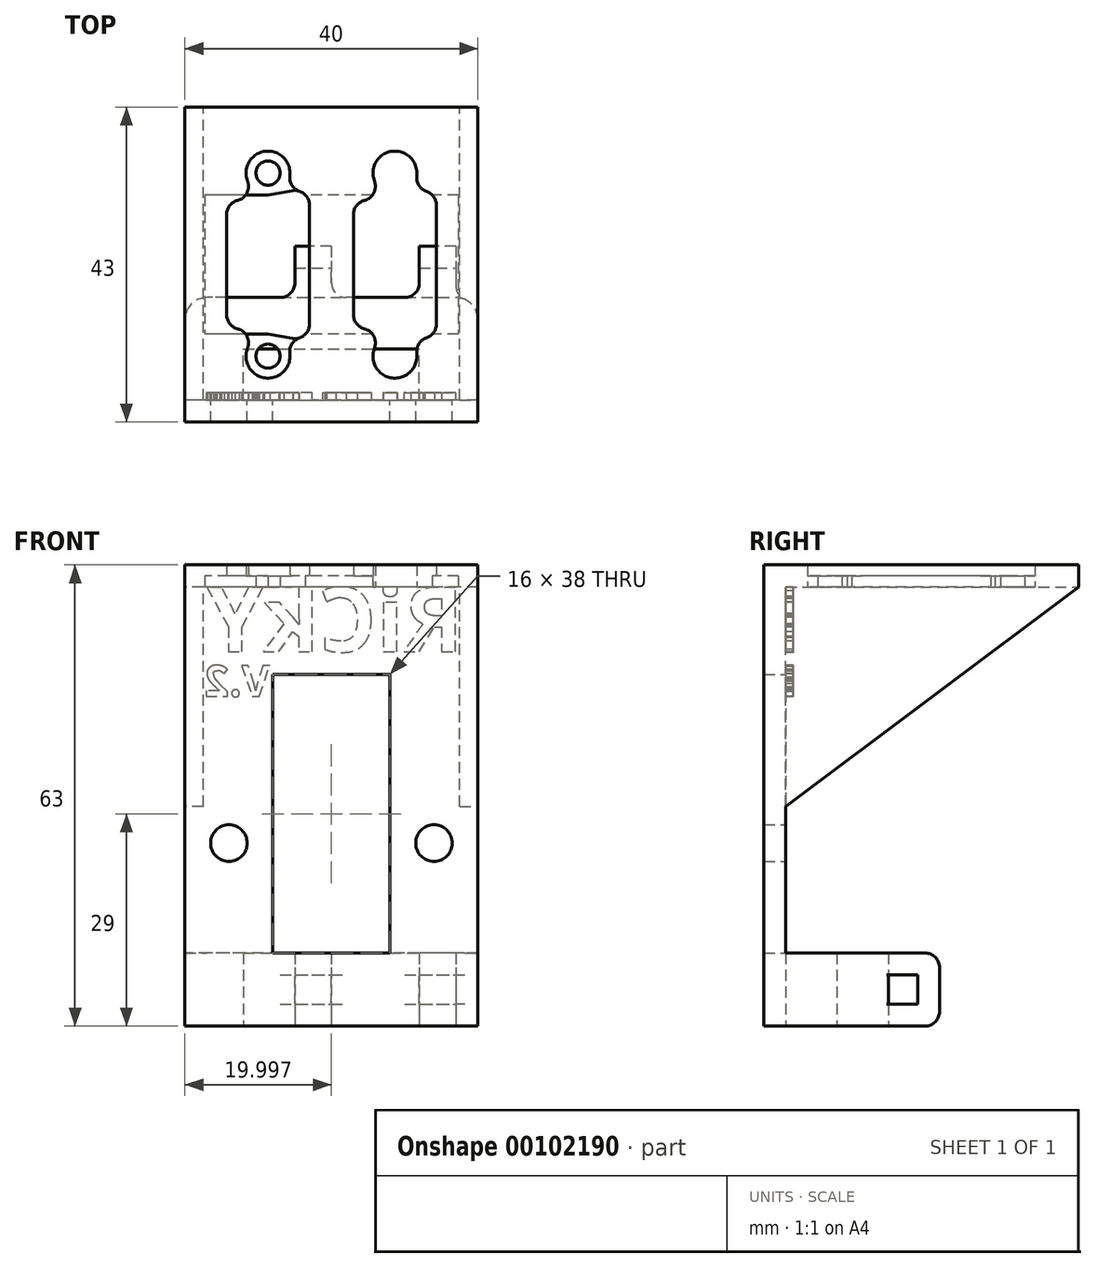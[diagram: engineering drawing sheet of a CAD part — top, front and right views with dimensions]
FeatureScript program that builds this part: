
annotation { "Feature Type Name" : "Feature", "Feature Type Description" : "" }
export const myFeature = defineFeature(function(context is Context, id is Id, definition is map)
    precondition{}
    {
        {
            var Q0;
            Q0=qCreatedBy(makeId("Top.planeOp"),FACE);
            var sketch = newSketch(context, id + "F0", { "sketchPlane" : qUnion([Q0])});
            skLineSegment(sketch, "E0", {"start": v(-4.26, 15.16) * mm, "end": v(16.74, 15.16) * mm});
            skLineSegment(sketch, "E1", {"start": v(-2.26, 3.83) * mm, "end": v(14.74, 3.83) * mm});
            skLineSegment(sketch, "E2", {"start": v(14.74, 3.83) * mm, "end": v(16.74, 15.16) * mm});
            skLineSegment(sketch, "E3", {"start": v(-2.26, 3.83) * mm, "end": v(-4.26, 15.16) * mm});
            skPoint(sketch, "E4", {"position": v(-3.26, 9.5) * mm});
            skPoint(sketch, "E5", {"position": v(15.74, 9.5) * mm});
            skPoint(sketch, "E6", {"position": v(-6.26, 9.5) * mm});
            skPoint(sketch, "E7", {"position": v(18.74, 9.5) * mm});
            skCircle(sketch, "E8", {"center": v(-6.26, 9.5) * mm, "radius": 3 * mm});
            skCircle(sketch, "E9", {"center": v(18.74, 9.5) * mm, "radius": 3 * mm});
            skLineSegment(sketch, "E10", {"start": v(-4.26, 32.48) * mm, "end": v(16.74, 32.48) * mm});
            skLineSegment(sketch, "E11", {"start": v(-2.26, 21.16) * mm, "end": v(14.74, 21.16) * mm});
            skLineSegment(sketch, "E12", {"start": v(14.74, 21.16) * mm, "end": v(16.74, 32.48) * mm});
            skLineSegment(sketch, "E13", {"start": v(-2.26, 21.16) * mm, "end": v(-4.26, 32.48) * mm});
            skPoint(sketch, "E14", {"position": v(-3.26, 26.82) * mm});
            skPoint(sketch, "E15", {"position": v(15.74, 26.82) * mm});
            skPoint(sketch, "E16", {"position": v(-6.26, 26.82) * mm});
            skPoint(sketch, "E17", {"position": v(18.74, 26.82) * mm});
            skCircle(sketch, "E18", {"center": v(-6.26, 26.82) * mm, "radius": 3 * mm});
            skCircle(sketch, "E19", {"center": v(18.74, 26.82) * mm, "radius": 3 * mm});
            skLineSegment(sketch, "E20.bottom", {"start": v(27.74, 38.16) * mm, "end": v(-15.26, 38.16) * mm});
            skLineSegment(sketch, "E20.top", {"start": v(27.74, -1.84) * mm, "end": v(-15.26, -1.84) * mm});
            skLineSegment(sketch, "E20.left", {"start": v(27.74, 38.16) * mm, "end": v(27.74, -1.84) * mm});
            skLineSegment(sketch, "E20.right", {"start": v(-15.26, 38.16) * mm, "end": v(-15.26, -1.84) * mm});
            skLineSegment(sketch, "E21", {"start": v(-6.26, 12.5) * mm, "end": v(-3.8, 12.5) * mm});
            skLineSegment(sketch, "E22", {"start": v(-6.26, 6.5) * mm, "end": v(-2.73, 6.5) * mm});
            skLineSegment(sketch, "E23", {"start": v(18.74, 12.5) * mm, "end": v(16.27, 12.5) * mm});
            skLineSegment(sketch, "E24", {"start": v(18.74, 6.5) * mm, "end": v(15.2, 6.5) * mm});
            skLineSegment(sketch, "E25", {"start": v(18.74, 29.82) * mm, "end": v(16.27, 29.82) * mm});
            skLineSegment(sketch, "E26", {"start": v(18.74, 23.82) * mm, "end": v(15.2, 23.82) * mm});
            skLineSegment(sketch, "E27", {"start": v(-6.26, 29.82) * mm, "end": v(-3.8, 29.82) * mm});
            skLineSegment(sketch, "E28", {"start": v(-6.26, 23.82) * mm, "end": v(-2.73, 23.82) * mm});
            skSolve(sketch);
        }
        {
            var Q0;
            Q0=makeQuery(id+"F0.imprint","IMPRINT",FACE,{"disambiguationData":[TD([[makeQuery(id+"F0.imprint","IMPRINT",EDGE,{"derivedFrom":sQuery(id+"F0.wireOp",EDGE,"E0")}),1.0]])]});
            var Q1;
            {var subQ0=sQuery(id+"F0.wireOp",EDGE,"E26");Q1=makeQuery(id+"F0.imprint","IMPRINT",FACE,{"disambiguationData":[TD([[makeQuery(id+"F0.imprint","IMPRINT",EDGE,{"derivedFrom":subQ0}),-1.0]])]});}
            var Q2;
            {var subQ0=sQuery(id+"F0.wireOp",EDGE,"E25");Q2=makeQuery(id+"F0.imprint","IMPRINT",FACE,{"disambiguationData":[TD([[makeQuery(id+"F0.imprint","IMPRINT",EDGE,{"derivedFrom":subQ0}),1.0]])]});}
            var Q3;
            {var subQ0=sQuery(id+"F0.wireOp",EDGE,"E24");Q3=makeQuery(id+"F0.imprint","IMPRINT",FACE,{"disambiguationData":[TD([[makeQuery(id+"F0.imprint","IMPRINT",EDGE,{"derivedFrom":subQ0}),-1.0]])]});}
            var Q4;
            {var subQ0=sQuery(id+"F0.wireOp",EDGE,"E23");Q4=makeQuery(id+"F0.imprint","IMPRINT",FACE,{"disambiguationData":[TD([[makeQuery(id+"F0.imprint","IMPRINT",EDGE,{"derivedFrom":subQ0}),1.0]])]});}
            var Q5;
            {var subQ0=sQuery(id+"F0.wireOp",EDGE,"E28");Q5=makeQuery(id+"F0.imprint","IMPRINT",FACE,{"disambiguationData":[TD([[makeQuery(id+"F0.imprint","IMPRINT",EDGE,{"derivedFrom":subQ0}),1.0]])]});}
            var Q6;
            {var subQ0=sQuery(id+"F0.wireOp",EDGE,"E27");Q6=makeQuery(id+"F0.imprint","IMPRINT",FACE,{"disambiguationData":[TD([[makeQuery(id+"F0.imprint","IMPRINT",EDGE,{"derivedFrom":subQ0}),-1.0]])]});}
            var Q7;
            {var subQ0=sQuery(id+"F0.wireOp",EDGE,"E22");Q7=makeQuery(id+"F0.imprint","IMPRINT",FACE,{"disambiguationData":[TD([[makeQuery(id+"F0.imprint","IMPRINT",EDGE,{"derivedFrom":subQ0}),1.0]])]});}
            var Q8;
            {var subQ0=sQuery(id+"F0.wireOp",EDGE,"E21");Q8=makeQuery(id+"F0.imprint","IMPRINT",FACE,{"disambiguationData":[TD([[makeQuery(id+"F0.imprint","IMPRINT",EDGE,{"derivedFrom":subQ0}),-1.0]])]});}
            extrude(context, id + "F1", {"entities" : qUnion([Q0, Q1, Q2, Q3, Q4, Q5, Q6, Q7, Q8]), "depth" : 3 * mm});
        }
        {
            var Q0;
            Q0=makeQuery(id+"F1.opExtrude","SWEPT_EDGE",EDGE,{"disambiguationData":[OSD([sQuery(id+"F0.wireOp",EDGE,"E0"),sQuery(id+"F0.wireOp",EDGE,"E3")])]});
            var Q1;
            Q1=makeQuery(id+"F1.opExtrude","SWEPT_EDGE",EDGE,{"disambiguationData":[OSD([sQuery(id+"F0.wireOp",EDGE,"E1"),sQuery(id+"F0.wireOp",EDGE,"E2")])]});
            var Q2;
            Q2=makeQuery(id+"F1.opExtrude","SWEPT_EDGE",EDGE,{"disambiguationData":[OSD([sQuery(id+"F0.wireOp",EDGE,"E0"),sQuery(id+"F0.wireOp",EDGE,"E2")])]});
            var Q3;
            Q3=makeQuery(id+"F1.opExtrude","SWEPT_EDGE",EDGE,{"disambiguationData":[OSD([sQuery(id+"F0.wireOp",EDGE,"E1"),sQuery(id+"F0.wireOp",EDGE,"E3")])]});
            var Q4;
            Q4=makeQuery(id+"F1.opExtrude","SWEPT_EDGE",EDGE,{"disambiguationData":[OSD([sQuery(id+"F0.wireOp",EDGE,"E10"),sQuery(id+"F0.wireOp",EDGE,"E13")])]});
            var Q5;
            Q5=makeQuery(id+"F1.opExtrude","SWEPT_EDGE",EDGE,{"disambiguationData":[OSD([sQuery(id+"F0.wireOp",EDGE,"E10"),sQuery(id+"F0.wireOp",EDGE,"E12")])]});
            var Q6;
            Q6=makeQuery(id+"F1.opExtrude","SWEPT_EDGE",EDGE,{"disambiguationData":[OSD([sQuery(id+"F0.wireOp",EDGE,"E11"),sQuery(id+"F0.wireOp",EDGE,"E13")])]});
            var Q7;
            Q7=makeQuery(id+"F1.opExtrude","SWEPT_EDGE",EDGE,{"disambiguationData":[OSD([sQuery(id+"F0.wireOp",EDGE,"E11"),sQuery(id+"F0.wireOp",EDGE,"E12")])]});
            var Q8;
            Q8=makeQuery(id+"F1.opExtrude","SWEPT_EDGE",EDGE,{"disambiguationData":[OSD([sQuery(id+"F0.wireOp",EDGE,"f29082a4-7322-47cb-b465-19e4ea49e02b"),sQuery(id+"F0.wireOp",EDGE,"14dc6c6a-b0b1-46ac-8881-e0cf73ac1d2b")])]});
            var Q9;
            Q9=makeQuery(id+"F1.opExtrude","SWEPT_EDGE",EDGE,{"disambiguationData":[OSD([sQuery(id+"F0.wireOp",EDGE,"37bfe060-5fdc-4ec3-b687-e42349816e1c"),sQuery(id+"F0.wireOp",EDGE,"0510f65d-9c0c-41d7-9503-72beef485745")])]});
            var Q10;
            Q10=makeQuery(id+"F1.opExtrude","SWEPT_EDGE",EDGE,{"disambiguationData":[OSD([sQuery(id+"F0.wireOp",EDGE,"48f8643b-9231-434c-8d4f-c31493e6ee47"),sQuery(id+"F0.wireOp",EDGE,"14dc6c6a-b0b1-46ac-8881-e0cf73ac1d2b")])]});
            var Q11;
            Q11=makeQuery(id+"F1.opExtrude","SWEPT_EDGE",EDGE,{"disambiguationData":[OSD([sQuery(id+"F0.wireOp",EDGE,"48f8643b-9231-434c-8d4f-c31493e6ee47"),sQuery(id+"F0.wireOp",EDGE,"811e4e27-a576-4234-9d9e-99fd6e5ff174")])]});
            var Q12;
            Q12=makeQuery(id+"F1.opExtrude","SWEPT_EDGE",EDGE,{"disambiguationData":[OSD([sQuery(id+"F0.wireOp",EDGE,"37bfe060-5fdc-4ec3-b687-e42349816e1c"),sQuery(id+"F0.wireOp",EDGE,"e401b783-9b0b-468a-a8fa-19b962c110bf")])]});
            var Q13;
            Q13=makeQuery(id+"F1.opExtrude","SWEPT_EDGE",EDGE,{"disambiguationData":[OSD([sQuery(id+"F0.wireOp",EDGE,"f29082a4-7322-47cb-b465-19e4ea49e02b"),sQuery(id+"F0.wireOp",EDGE,"811e4e27-a576-4234-9d9e-99fd6e5ff174")])]});
            var Q14;
            Q14=makeQuery(id+"F1.opExtrude","SWEPT_EDGE",EDGE,{"disambiguationData":[OSD([sQuery(id+"F0.wireOp",EDGE,"dc5348c1-fa33-4584-8c39-a4fec2a28e45"),sQuery(id+"F0.wireOp",EDGE,"e401b783-9b0b-468a-a8fa-19b962c110bf")])]});
            var Q15;
            Q15=makeQuery(id+"F1.opExtrude","SWEPT_EDGE",EDGE,{"disambiguationData":[OSD([sQuery(id+"F0.wireOp",EDGE,"dc5348c1-fa33-4584-8c39-a4fec2a28e45"),sQuery(id+"F0.wireOp",EDGE,"0510f65d-9c0c-41d7-9503-72beef485745")])]});
            fillet(context, id + "F2", {"entities" : qUnion([Q0, Q1, Q2, Q3, Q4, Q5, Q6, Q7, Q8, Q9, Q10, Q11, Q12, Q13, Q14, Q15]), "radius" : 2 * mm, "tangentPropagation" : true, "allowEdgeOverflow" : false});
        }
        {
            var Q0;
            Q0=makeQuery(id+"F0.imprint","IMPRINT",FACE,{"disambiguationData":[TD([[makeQuery(id+"F0.imprint","IMPRINT",EDGE,{"derivedFrom":sQuery(id+"F0.wireOp",EDGE,"E8")}),1.0]])]});
            var Q1;
            Q1=makeQuery(id+"F0.imprint","IMPRINT",FACE,{"disambiguationData":[TD([[makeQuery(id+"F0.imprint","IMPRINT",EDGE,{"derivedFrom":sQuery(id+"F0.wireOp",EDGE,"E9")}),1.0]])]});
            var Q2;
            {var subQ0=sQuery(id+"F0.wireOp",EDGE,"E18");var subQ1=sQuery(id+"F0.wireOp",EDGE,"E13");var subQ2=makeQuery(id+"F0.imprint","INTERSECT",VERTEX,{"disambiguationData":[OD(0.0)],"derivedFrom":[subQ1,subQ0]});Q2=makeQuery(id+"F0.imprint","IMPRINT",FACE,{"disambiguationData":[TD([[makeQuery(id+"F0.imprint","IMPRINT",EDGE,{"disambiguationData":[TD([[subQ2,-1.0]])],"derivedFrom":subQ1}),1.0]])]});}
            var Q3;
            {var subQ0=sQuery(id+"F0.wireOp",EDGE,"E19");var subQ1=sQuery(id+"F0.wireOp",EDGE,"E12");var subQ2=makeQuery(id+"F0.imprint","INTERSECT",VERTEX,{"disambiguationData":[OD(0.0)],"derivedFrom":[subQ1,subQ0]});Q3=makeQuery(id+"F0.imprint","IMPRINT",FACE,{"disambiguationData":[TD([[makeQuery(id+"F0.imprint","IMPRINT",EDGE,{"disambiguationData":[TD([[subQ2,-1.0]])],"derivedFrom":subQ1}),-1.0]])]});}
            var Q4;
            {var subQ0=sQuery(id+"F0.wireOp",EDGE,"a1f57022-cb78-4938-9068-114398bfe586");var subQ1=sQuery(id+"F0.wireOp",EDGE,"14dc6c6a-b0b1-46ac-8881-e0cf73ac1d2b");var subQ2=makeQuery(id+"F0.imprint","INTERSECT",VERTEX,{"disambiguationData":[OD(0.0)],"derivedFrom":[subQ1,subQ0]});Q4=makeQuery(id+"F0.imprint","IMPRINT",FACE,{"disambiguationData":[TD([[makeQuery(id+"F0.imprint","IMPRINT",EDGE,{"disambiguationData":[TD([[subQ2,-1.0]])],"derivedFrom":subQ1}),-1.0]])]});}
            var Q5;
            {var subQ0=sQuery(id+"F0.wireOp",EDGE,"86ebaf99-70f6-4ba5-b64b-6db6493a615a");var subQ1=sQuery(id+"F0.wireOp",EDGE,"811e4e27-a576-4234-9d9e-99fd6e5ff174");var subQ2=makeQuery(id+"F0.imprint","INTERSECT",VERTEX,{"disambiguationData":[OD(0.0)],"derivedFrom":[subQ1,subQ0]});Q5=makeQuery(id+"F0.imprint","IMPRINT",FACE,{"disambiguationData":[TD([[makeQuery(id+"F0.imprint","IMPRINT",EDGE,{"disambiguationData":[TD([[subQ2,-1.0]])],"derivedFrom":subQ1}),1.0]])]});}
            var Q6;
            {var subQ0=sQuery(id+"F0.wireOp",EDGE,"cc97c6fd-5fec-4752-a4a8-6a94110f7a13");var subQ1=sQuery(id+"F0.wireOp",EDGE,"0510f65d-9c0c-41d7-9503-72beef485745");var subQ2=makeQuery(id+"F0.imprint","INTERSECT",VERTEX,{"disambiguationData":[OD(0.0)],"derivedFrom":[subQ1,subQ0]});Q6=makeQuery(id+"F0.imprint","IMPRINT",FACE,{"disambiguationData":[TD([[makeQuery(id+"F0.imprint","IMPRINT",EDGE,{"disambiguationData":[TD([[subQ2,-1.0]])],"derivedFrom":subQ1}),-1.0]])]});}
            var Q7;
            {var subQ0=sQuery(id+"F0.wireOp",EDGE,"1ddf9c7e-1f22-45b9-9486-a590a8503efe");var subQ1=sQuery(id+"F0.wireOp",EDGE,"e401b783-9b0b-468a-a8fa-19b962c110bf");var subQ2=makeQuery(id+"F0.imprint","INTERSECT",VERTEX,{"disambiguationData":[OD(0.0)],"derivedFrom":[subQ1,subQ0]});Q7=makeQuery(id+"F0.imprint","IMPRINT",FACE,{"disambiguationData":[TD([[makeQuery(id+"F0.imprint","IMPRINT",EDGE,{"disambiguationData":[TD([[subQ2,-1.0]])],"derivedFrom":subQ1}),1.0]])]});}
            var Q8;
            {var subQ0=sQuery(id+"F0.wireOp",EDGE,"nIp2yuOM-g37C-dqSd-L2FJ-qzEwNihu1C9F");Q8=makeQuery(id+"F0.imprint","IMPRINT",FACE,{"disambiguationData":[TD([[makeQuery(id+"F0.imprint","IMPRINT",EDGE,{"derivedFrom":subQ0}),1.0]])]});}
            var Q9;
            {var subQ0=sQuery(id+"F0.wireOp",EDGE,"wKLpr2SQ-OYyE-akfH-OegQ-YmX1uECdlRNC");Q9=makeQuery(id+"F0.imprint","IMPRINT",FACE,{"disambiguationData":[TD([[makeQuery(id+"F0.imprint","IMPRINT",EDGE,{"derivedFrom":subQ0}),-1.0]])]});}
            var Q10;
            {var subQ0=sQuery(id+"F0.wireOp",EDGE,"QdcXmw05-nOh7-w33V-2QU8-xGgOXz3l01cY");Q10=makeQuery(id+"F0.imprint","IMPRINT",FACE,{"disambiguationData":[TD([[makeQuery(id+"F0.imprint","IMPRINT",EDGE,{"derivedFrom":subQ0}),-1.0]])]});}
            var Q11;
            {var subQ0=sQuery(id+"F0.wireOp",EDGE,"vOi8BEkP-FgyD-ud1J-If9y-5dLZR6NiCd4x");Q11=makeQuery(id+"F0.imprint","IMPRINT",FACE,{"disambiguationData":[TD([[makeQuery(id+"F0.imprint","IMPRINT",EDGE,{"derivedFrom":subQ0}),1.0]])]});}
            var Q12;
            {var subQ0=sQuery(id+"F0.wireOp",EDGE,"uGGpDXvE-blJh-SpWV-2VnG-ZkKB8chZi5NL");Q12=makeQuery(id+"F0.imprint","IMPRINT",FACE,{"disambiguationData":[TD([[makeQuery(id+"F0.imprint","IMPRINT",EDGE,{"derivedFrom":subQ0}),-1.0]])]});}
            var Q13;
            {var subQ0=sQuery(id+"F0.wireOp",EDGE,"6a2Y8GzF-T0tt-Anft-jwha-FWHqF83FpDPI");Q13=makeQuery(id+"F0.imprint","IMPRINT",FACE,{"disambiguationData":[TD([[makeQuery(id+"F0.imprint","IMPRINT",EDGE,{"derivedFrom":subQ0}),1.0]])]});}
            var Q14;
            {var subQ0=sQuery(id+"F0.wireOp",EDGE,"dBvgyE4v-Y0vW-xrYq-FLgZ-j6EjYADPISw6");Q14=makeQuery(id+"F0.imprint","IMPRINT",FACE,{"disambiguationData":[TD([[makeQuery(id+"F0.imprint","IMPRINT",EDGE,{"derivedFrom":subQ0}),1.0]])]});}
            var Q15;
            {var subQ0=sQuery(id+"F0.wireOp",EDGE,"ugh5pSRK-4Ctj-t1Pz-bgVR-spiEpQOtgNRe");Q15=makeQuery(id+"F0.imprint","IMPRINT",FACE,{"disambiguationData":[TD([[makeQuery(id+"F0.imprint","IMPRINT",EDGE,{"derivedFrom":subQ0}),-1.0]])]});}
            var Q16;
            {var subQ0=sQuery(id+"F0.wireOp",EDGE,"E22");Q16=makeQuery(id+"F0.imprint","IMPRINT",FACE,{"disambiguationData":[TD([[makeQuery(id+"F0.imprint","IMPRINT",EDGE,{"derivedFrom":subQ0}),1.0]])]});}
            var Q17;
            {var subQ0=sQuery(id+"F0.wireOp",EDGE,"E21");Q17=makeQuery(id+"F0.imprint","IMPRINT",FACE,{"disambiguationData":[TD([[makeQuery(id+"F0.imprint","IMPRINT",EDGE,{"derivedFrom":subQ0}),-1.0]])]});}
            var Q18;
            {var subQ0=sQuery(id+"F0.wireOp",EDGE,"E24");Q18=makeQuery(id+"F0.imprint","IMPRINT",FACE,{"disambiguationData":[TD([[makeQuery(id+"F0.imprint","IMPRINT",EDGE,{"derivedFrom":subQ0}),-1.0]])]});}
            var Q19;
            {var subQ0=sQuery(id+"F0.wireOp",EDGE,"E23");Q19=makeQuery(id+"F0.imprint","IMPRINT",FACE,{"disambiguationData":[TD([[makeQuery(id+"F0.imprint","IMPRINT",EDGE,{"derivedFrom":subQ0}),1.0]])]});}
            var Q20;
            {var subQ0=sQuery(id+"F0.wireOp",EDGE,"E26");Q20=makeQuery(id+"F0.imprint","IMPRINT",FACE,{"disambiguationData":[TD([[makeQuery(id+"F0.imprint","IMPRINT",EDGE,{"derivedFrom":subQ0}),-1.0]])]});}
            var Q21;
            {var subQ0=sQuery(id+"F0.wireOp",EDGE,"E25");Q21=makeQuery(id+"F0.imprint","IMPRINT",FACE,{"disambiguationData":[TD([[makeQuery(id+"F0.imprint","IMPRINT",EDGE,{"derivedFrom":subQ0}),1.0]])]});}
            var Q22;
            {var subQ0=sQuery(id+"F0.wireOp",EDGE,"E27");Q22=makeQuery(id+"F0.imprint","IMPRINT",FACE,{"disambiguationData":[TD([[makeQuery(id+"F0.imprint","IMPRINT",EDGE,{"derivedFrom":subQ0}),-1.0]])]});}
            var Q23;
            {var subQ0=sQuery(id+"F0.wireOp",EDGE,"E28");Q23=makeQuery(id+"F0.imprint","IMPRINT",FACE,{"disambiguationData":[TD([[makeQuery(id+"F0.imprint","IMPRINT",EDGE,{"derivedFrom":subQ0}),1.0]])]});}
            extrude(context, id + "F3", {"entities" : qUnion([Q0, Q1, Q2, Q3, Q4, Q5, Q6, Q7, Q8, Q9, Q10, Q11, Q12, Q13, Q14, Q15, Q16, Q17, Q18, Q19, Q20, Q21, Q22, Q23]), "operationType" : NewBodyOperationType.ADD, "depth" : 1.5 * mm});
        }
        {
            var Q0;
            Q0=sQuery(id+"F0.wireOp",VERTEX,"E6");
            var Q1;
            Q1=sQuery(id+"F0.wireOp",VERTEX,"E7");
            var Q2;
            Q2=sQuery(id+"F0.wireOp",VERTEX,"E16");
            var Q3;
            Q3=sQuery(id+"F0.wireOp",VERTEX,"E17");
            var Q4;
            Q4=sQuery(id+"F0.wireOp",VERTEX,"0fdf1792-d076-4e39-9bfd-63a167ac2963");
            var Q5;
            Q5=sQuery(id+"F0.wireOp",VERTEX,"717df0d1-ba1e-4093-a840-74a35961894c");
            var Q6;
            Q6=sQuery(id+"F0.wireOp",VERTEX,"da223fd1-ca9d-4154-b710-04e4a6dde9f6");
            var Q7;
            Q7=sQuery(id+"F0.wireOp",VERTEX,"32cd1edf-c6c8-4931-b3ad-bf64c6211db5");
            var Q8;
            Q8=makeQuery(id+"F1.opExtrude","SWEPT_BODY",BODY,{"disambiguationData":[OSD([sQuery(id+"F0.wireOp",EDGE,"E0"),sQuery(id+"F0.wireOp",EDGE,"E1"),sQuery(id+"F0.wireOp",EDGE,"E2"),sQuery(id+"F0.wireOp",EDGE,"E3"),sQuery(id+"F0.wireOp",EDGE,"Wovf68Om-m2Ft-W6fg-vgO9-NATX11qrs2Ft.bottom"),sQuery(id+"F0.wireOp",EDGE,"Wovf68Om-m2Ft-W6fg-vgO9-NATX11qrs2Ft.top"),sQuery(id+"F0.wireOp",EDGE,"Wovf68Om-m2Ft-W6fg-vgO9-NATX11qrs2Ft.left"),sQuery(id+"F0.wireOp",EDGE,"Wovf68Om-m2Ft-W6fg-vgO9-NATX11qrs2Ft.right")])]});
            hole(context, id + "F4", {"style" : HoleStyle.SIMPLE, "endStyle" : HoleEndStyle.THROUGH, "oppositeDirection" : true, "holeDiameter" : 3.3 * mm, "startFromSketch" : true, "locations" : qUnion([Q0, Q1, Q2, Q3, Q4, Q5, Q6, Q7]), "scope" : qUnion([Q8]), "isTappedThrough" : true});
        }
        {
            var Q0;
            {var subQ0=sQuery(id+"F0.wireOp",EDGE,"1ddf9c7e-1f22-45b9-9486-a590a8503efe");var subQ1=sQuery(id+"F0.wireOp",EDGE,"e401b783-9b0b-468a-a8fa-19b962c110bf");var subQ2=sQuery(id+"F0.wireOp",EDGE,"cc97c6fd-5fec-4752-a4a8-6a94110f7a13");var subQ3=sQuery(id+"F0.wireOp",EDGE,"0510f65d-9c0c-41d7-9503-72beef485745");var subQ4=sQuery(id+"F0.wireOp",EDGE,"E18");var subQ5=sQuery(id+"F0.wireOp",EDGE,"E13");var subQ6=sQuery(id+"F0.wireOp",EDGE,"E19");var subQ7=sQuery(id+"F0.wireOp",EDGE,"E12");var subQ8=sQuery(id+"F0.wireOp",EDGE,"86ebaf99-70f6-4ba5-b64b-6db6493a615a");var subQ9=sQuery(id+"F0.wireOp",EDGE,"811e4e27-a576-4234-9d9e-99fd6e5ff174");var subQ10=sQuery(id+"F0.wireOp",EDGE,"a1f57022-cb78-4938-9068-114398bfe586");var subQ11=sQuery(id+"F0.wireOp",EDGE,"14dc6c6a-b0b1-46ac-8881-e0cf73ac1d2b");var subQ12=sQuery(id+"F0.wireOp",EDGE,"E9");var subQ13=sQuery(id+"F0.wireOp",EDGE,"E8");Q0=makeQuery(id+"F3.boolean.opBoolean","MERGE",FACE,{"derivedFrom":[makeQuery(id+"F1.opExtrude","CAP_FACE",FACE,{"disambiguationData":[OSD([sQuery(id+"F0.wireOp",EDGE,"E0"),sQuery(id+"F0.wireOp",EDGE,"E1"),sQuery(id+"F0.wireOp",EDGE,"E2"),sQuery(id+"F0.wireOp",EDGE,"E3"),subQ13,subQ12,sQuery(id+"F0.wireOp",EDGE,"48f8643b-9231-434c-8d4f-c31493e6ee47"),sQuery(id+"F0.wireOp",EDGE,"f29082a4-7322-47cb-b465-19e4ea49e02b"),subQ11,subQ9,subQ8,subQ10,sQuery(id+"F0.wireOp",EDGE,"E10"),sQuery(id+"F0.wireOp",EDGE,"E11"),subQ7,subQ5,subQ4,subQ6,sQuery(id+"F0.wireOp",EDGE,"E20.bottom"),sQuery(id+"F0.wireOp",EDGE,"E20.top"),sQuery(id+"F0.wireOp",EDGE,"E20.left"),sQuery(id+"F0.wireOp",EDGE,"E20.right"),sQuery(id+"F0.wireOp",EDGE,"37bfe060-5fdc-4ec3-b687-e42349816e1c"),sQuery(id+"F0.wireOp",EDGE,"dc5348c1-fa33-4584-8c39-a4fec2a28e45"),subQ3,subQ1,subQ0,subQ2])],"isStart":true}),makeQuery(id+"F3.opExtrude","CAP_FACE",FACE,{"disambiguationData":[OSD([subQ13])],"isStart":true}),makeQuery(id+"F3.opExtrude","CAP_FACE",FACE,{"disambiguationData":[OSD([subQ12])],"isStart":true}),makeQuery(id+"F3.opExtrude","CAP_FACE",FACE,{"disambiguationData":[OSD([subQ11,subQ10])],"isStart":true}),makeQuery(id+"F3.opExtrude","CAP_FACE",FACE,{"disambiguationData":[OSD([subQ9,subQ8])],"isStart":true}),makeQuery(id+"F3.opExtrude","CAP_FACE",FACE,{"disambiguationData":[OSD([subQ7,subQ6])],"isStart":true}),makeQuery(id+"F3.opExtrude","CAP_FACE",FACE,{"disambiguationData":[OSD([subQ5,subQ4])],"isStart":true}),makeQuery(id+"F3.opExtrude","CAP_FACE",FACE,{"disambiguationData":[OSD([subQ3,subQ2])],"isStart":true}),makeQuery(id+"F3.opExtrude","CAP_FACE",FACE,{"disambiguationData":[OSD([subQ1,subQ0])],"isStart":true})]});}
            var sketch = newSketch(context, id + "F5", { "sketchPlane" : qUnion([Q0])});
            skLineSegment(sketch, "E29.bottom", {"start": v(24.74, -38.16) * mm, "end": v(27.74, -38.16) * mm});
            skLineSegment(sketch, "E29.top", {"start": v(24.74, 1.84) * mm, "end": v(27.74, 1.84) * mm});
            skLineSegment(sketch, "E29.left", {"start": v(24.74, -38.16) * mm, "end": v(24.74, 1.84) * mm});
            skLineSegment(sketch, "E29.right", {"start": v(27.74, -38.16) * mm, "end": v(27.74, 1.84) * mm});
            skSolve(sketch);
        }
        {
            var Q0;
            Q0=makeQuery(id+"F5.imprint","IMPRINT",FACE,{"disambiguationData":[TD([[makeQuery(id+"F5.imprint","IMPRINT",EDGE,{"derivedFrom":sQuery(id+"F5.wireOp",EDGE,"E29.bottom")}),-1.0]])]});
            extrude(context, id + "F6", {"entities" : qUnion([Q0]), "operationType" : NewBodyOperationType.ADD, "depth" : 60 * mm});
        }
        {
            var Q0;
            Q0=makeQuery(id+"F6.boolean.opBoolean","MERGE",FACE,{"derivedFrom":[makeQuery(id+"F1.opExtrude","SWEPT_FACE",FACE,{"disambiguationData":[OSD([sQuery(id+"F0.wireOp",EDGE,"E20.bottom")])]}),makeQuery(id+"F6.opExtrude","SWEPT_FACE",FACE,{"disambiguationData":[OSD([sQuery(id+"F5.wireOp",EDGE,"E29.bottom")])]})]});
            var sketch = newSketch(context, id + "F7", { "sketchPlane" : qUnion([Q0])});
            skLineSegment(sketch, "E30", {"start": v(15.26, 0) * mm, "end": v(-24.74, -30) * mm});
            skLineSegment(sketch, "E31", {"start": v(-24.74, -30) * mm, "end": v(-24.74, 0) * mm});
            skLineSegment(sketch, "E32", {"start": v(-24.74, 0) * mm, "end": v(15.26, 0) * mm});
            skSolve(sketch);
        }
        {
            var Q0;
            Q0=makeQuery(id+"F6.boolean.opBoolean","MERGE",FACE,{"derivedFrom":[makeQuery(id+"F1.opExtrude","SWEPT_FACE",FACE,{"disambiguationData":[OSD([sQuery(id+"F0.wireOp",EDGE,"E20.top")])]}),makeQuery(id+"F6.opExtrude","SWEPT_FACE",FACE,{"disambiguationData":[OSD([sQuery(id+"F5.wireOp",EDGE,"E29.top")])]})]});
            var sketch = newSketch(context, id + "F8", { "sketchPlane" : qUnion([Q0])});
            skLineSegment(sketch, "E33", {"start": v(-15.26, 0) * mm, "end": v(24.74, -30) * mm});
            skSolve(sketch);
        }
        {
            var Q0;
            Q0=makeQuery(id+"F7.imprint","IMPRINT",FACE,{"disambiguationData":[TD([[makeQuery(id+"F7.imprint","IMPRINT",EDGE,{"derivedFrom":sQuery(id+"F7.wireOp",EDGE,"E30")}),-1.0]])]});
            extrude(context, id + "F9", {"entities" : qUnion([Q0]), "operationType" : NewBodyOperationType.ADD, "oppositeDirection" : true, "depth" : 2 * mm});
        }
        {
            var Q0;
            {var subQ0=sQuery(id+"F8.wireOp",EDGE,"E33");Q0=makeQuery(id+"F8.imprint","IMPRINT",FACE,{"disambiguationData":[TD([[makeQuery(id+"F8.imprint","IMPRINT",EDGE,{"derivedFrom":subQ0}),1.0]])]});}
            extrude(context, id + "F10", {"entities" : qUnion([Q0]), "operationType" : NewBodyOperationType.ADD, "oppositeDirection" : true, "depth" : 2 * mm});
        }
        {
            var Q0;
            Q0=makeQuery(id+"F6.opExtrude","SWEPT_FACE",FACE,{"disambiguationData":[OSD([sQuery(id+"F5.wireOp",EDGE,"E29.left")])]});
            var sketch = newSketch(context, id + "F11", { "sketchPlane" : qUnion([Q0])});
            skLineSegment(sketch, "E34.bottom", {"start": v(-26.16, -12) * mm, "end": v(-10.16, -12) * mm});
            skLineSegment(sketch, "E34.top", {"start": v(-26.16, -52) * mm, "end": v(-10.16, -52) * mm});
            skLineSegment(sketch, "E34.left", {"start": v(-26.16, -12) * mm, "end": v(-26.16, -52) * mm});
            skLineSegment(sketch, "E34.right", {"start": v(-10.16, -12) * mm, "end": v(-10.16, -52) * mm});
            skPoint(sketch, "E35.positionSnap0", {"position": v(-18.16, 0) * mm});
            skSolve(sketch);
        }
        {
            var Q0;
            Q0=makeQuery(id+"F11.imprint","IMPRINT",FACE,{"disambiguationData":[TD([[makeQuery(id+"F11.imprint","IMPRINT",EDGE,{"derivedFrom":sQuery(id+"F11.wireOp",EDGE,"E34.bottom")}),-1.0]])]});
            extrude(context, id + "F12", {"entities" : qUnion([Q0]), "operationType" : NewBodyOperationType.REMOVE, "oppositeDirection" : true, "depth" : 3 * mm});
        }
        {
            var Q0;
            Q0=makeQuery(id+"F1.opExtrude","SWEPT_EDGE",EDGE,{"disambiguationData":[OSD([sQuery(id+"F0.wireOp",EDGE,"e401b783-9b0b-468a-a8fa-19b962c110bf"),sQuery(id+"F0.wireOp",EDGE,"nIp2yuOM-g37C-dqSd-L2FJ-qzEwNihu1C9F")])]});
            var Q1;
            Q1=makeQuery(id+"F1.opExtrude","SWEPT_EDGE",EDGE,{"disambiguationData":[OSD([sQuery(id+"F0.wireOp",EDGE,"e401b783-9b0b-468a-a8fa-19b962c110bf"),sQuery(id+"F0.wireOp",EDGE,"wKLpr2SQ-OYyE-akfH-OegQ-YmX1uECdlRNC")])]});
            var Q2;
            Q2=makeQuery(id+"F1.opExtrude","SWEPT_EDGE",EDGE,{"disambiguationData":[OSD([sQuery(id+"F0.wireOp",EDGE,"0510f65d-9c0c-41d7-9503-72beef485745"),sQuery(id+"F0.wireOp",EDGE,"QdcXmw05-nOh7-w33V-2QU8-xGgOXz3l01cY")])]});
            var Q3;
            Q3=makeQuery(id+"F1.opExtrude","SWEPT_EDGE",EDGE,{"disambiguationData":[OSD([sQuery(id+"F0.wireOp",EDGE,"0510f65d-9c0c-41d7-9503-72beef485745"),sQuery(id+"F0.wireOp",EDGE,"vOi8BEkP-FgyD-ud1J-If9y-5dLZR6NiCd4x")])]});
            var Q4;
            Q4=makeQuery(id+"F1.opExtrude","SWEPT_EDGE",EDGE,{"disambiguationData":[OSD([sQuery(id+"F0.wireOp",EDGE,"14dc6c6a-b0b1-46ac-8881-e0cf73ac1d2b"),sQuery(id+"F0.wireOp",EDGE,"6a2Y8GzF-T0tt-Anft-jwha-FWHqF83FpDPI")])]});
            var Q5;
            Q5=makeQuery(id+"F1.opExtrude","SWEPT_EDGE",EDGE,{"disambiguationData":[OSD([sQuery(id+"F0.wireOp",EDGE,"811e4e27-a576-4234-9d9e-99fd6e5ff174"),sQuery(id+"F0.wireOp",EDGE,"ugh5pSRK-4Ctj-t1Pz-bgVR-spiEpQOtgNRe")])]});
            var Q6;
            Q6=makeQuery(id+"F1.opExtrude","SWEPT_EDGE",EDGE,{"disambiguationData":[OSD([sQuery(id+"F0.wireOp",EDGE,"811e4e27-a576-4234-9d9e-99fd6e5ff174"),sQuery(id+"F0.wireOp",EDGE,"dBvgyE4v-Y0vW-xrYq-FLgZ-j6EjYADPISw6")])]});
            var Q7;
            Q7=makeQuery(id+"F1.opExtrude","SWEPT_EDGE",EDGE,{"disambiguationData":[OSD([sQuery(id+"F0.wireOp",EDGE,"14dc6c6a-b0b1-46ac-8881-e0cf73ac1d2b"),sQuery(id+"F0.wireOp",EDGE,"uGGpDXvE-blJh-SpWV-2VnG-ZkKB8chZi5NL")])]});
            var Q8;
            Q8=makeQuery(id+"F1.opExtrude","SWEPT_EDGE",EDGE,{"disambiguationData":[OSD([sQuery(id+"F0.wireOp",EDGE,"E3"),sQuery(id+"F0.wireOp",EDGE,"E22")])]});
            var Q9;
            Q9=makeQuery(id+"F1.opExtrude","SWEPT_EDGE",EDGE,{"disambiguationData":[OSD([sQuery(id+"F0.wireOp",EDGE,"E2"),sQuery(id+"F0.wireOp",EDGE,"E24")])]});
            var Q10;
            Q10=makeQuery(id+"F1.opExtrude","SWEPT_EDGE",EDGE,{"disambiguationData":[OSD([sQuery(id+"F0.wireOp",EDGE,"E12"),sQuery(id+"F0.wireOp",EDGE,"E26")])]});
            var Q11;
            Q11=makeQuery(id+"F1.opExtrude","SWEPT_EDGE",EDGE,{"disambiguationData":[OSD([sQuery(id+"F0.wireOp",EDGE,"E13"),sQuery(id+"F0.wireOp",EDGE,"E28")])]});
            var Q12;
            Q12=makeQuery(id+"F1.opExtrude","SWEPT_EDGE",EDGE,{"disambiguationData":[OSD([sQuery(id+"F0.wireOp",EDGE,"E3"),sQuery(id+"F0.wireOp",EDGE,"E21")])]});
            var Q13;
            Q13=makeQuery(id+"F1.opExtrude","SWEPT_EDGE",EDGE,{"disambiguationData":[OSD([sQuery(id+"F0.wireOp",EDGE,"E2"),sQuery(id+"F0.wireOp",EDGE,"E23")])]});
            var Q14;
            Q14=makeQuery(id+"F1.opExtrude","SWEPT_EDGE",EDGE,{"disambiguationData":[OSD([sQuery(id+"F0.wireOp",EDGE,"E12"),sQuery(id+"F0.wireOp",EDGE,"E25")])]});
            var Q15;
            Q15=makeQuery(id+"F1.opExtrude","SWEPT_EDGE",EDGE,{"disambiguationData":[OSD([sQuery(id+"F0.wireOp",EDGE,"E13"),sQuery(id+"F0.wireOp",EDGE,"E27")])]});
            fillet(context, id + "F13", {"entities" : qUnion([Q0, Q1, Q2, Q3, Q4, Q5, Q6, Q7, Q8, Q9, Q10, Q11, Q12, Q13, Q14, Q15]), "radius" : 2 * mm, "tangentPropagation" : true, "allowEdgeOverflow" : false});
        }
        {
            var Q0;
            Q0=makeQuery(id+"F1.opExtrude","SWEPT_BODY",BODY,{"disambiguationData":[OSD([sQuery(id+"F0.wireOp",EDGE,"E0"),sQuery(id+"F0.wireOp",EDGE,"E1"),sQuery(id+"F0.wireOp",EDGE,"E2"),sQuery(id+"F0.wireOp",EDGE,"E3"),sQuery(id+"F0.wireOp",EDGE,"E8"),sQuery(id+"F0.wireOp",EDGE,"E9"),sQuery(id+"F0.wireOp",EDGE,"48f8643b-9231-434c-8d4f-c31493e6ee47"),sQuery(id+"F0.wireOp",EDGE,"f29082a4-7322-47cb-b465-19e4ea49e02b"),sQuery(id+"F0.wireOp",EDGE,"14dc6c6a-b0b1-46ac-8881-e0cf73ac1d2b"),sQuery(id+"F0.wireOp",EDGE,"811e4e27-a576-4234-9d9e-99fd6e5ff174"),sQuery(id+"F0.wireOp",EDGE,"86ebaf99-70f6-4ba5-b64b-6db6493a615a"),sQuery(id+"F0.wireOp",EDGE,"a1f57022-cb78-4938-9068-114398bfe586"),sQuery(id+"F0.wireOp",EDGE,"E10"),sQuery(id+"F0.wireOp",EDGE,"E11"),sQuery(id+"F0.wireOp",EDGE,"E12"),sQuery(id+"F0.wireOp",EDGE,"E13"),sQuery(id+"F0.wireOp",EDGE,"E18"),sQuery(id+"F0.wireOp",EDGE,"E19"),sQuery(id+"F0.wireOp",EDGE,"E20.bottom"),sQuery(id+"F0.wireOp",EDGE,"E20.top"),sQuery(id+"F0.wireOp",EDGE,"E20.left"),sQuery(id+"F0.wireOp",EDGE,"E20.right"),sQuery(id+"F0.wireOp",EDGE,"37bfe060-5fdc-4ec3-b687-e42349816e1c"),sQuery(id+"F0.wireOp",EDGE,"dc5348c1-fa33-4584-8c39-a4fec2a28e45"),sQuery(id+"F0.wireOp",EDGE,"0510f65d-9c0c-41d7-9503-72beef485745"),sQuery(id+"F0.wireOp",EDGE,"e401b783-9b0b-468a-a8fa-19b962c110bf"),sQuery(id+"F0.wireOp",EDGE,"1ddf9c7e-1f22-45b9-9486-a590a8503efe"),sQuery(id+"F0.wireOp",EDGE,"cc97c6fd-5fec-4752-a4a8-6a94110f7a13"),sQuery(id+"F0.wireOp",EDGE,"E21"),sQuery(id+"F0.wireOp",EDGE,"E22"),sQuery(id+"F0.wireOp",EDGE,"E23"),sQuery(id+"F0.wireOp",EDGE,"E24"),sQuery(id+"F0.wireOp",EDGE,"E25"),sQuery(id+"F0.wireOp",EDGE,"E26"),sQuery(id+"F0.wireOp",EDGE,"E27"),sQuery(id+"F0.wireOp",EDGE,"E28"),sQuery(id+"F0.wireOp",EDGE,"ugh5pSRK-4Ctj-t1Pz-bgVR-spiEpQOtgNRe"),sQuery(id+"F0.wireOp",EDGE,"dBvgyE4v-Y0vW-xrYq-FLgZ-j6EjYADPISw6"),sQuery(id+"F0.wireOp",EDGE,"uGGpDXvE-blJh-SpWV-2VnG-ZkKB8chZi5NL"),sQuery(id+"F0.wireOp",EDGE,"6a2Y8GzF-T0tt-Anft-jwha-FWHqF83FpDPI"),sQuery(id+"F0.wireOp",EDGE,"vOi8BEkP-FgyD-ud1J-If9y-5dLZR6NiCd4x"),sQuery(id+"F0.wireOp",EDGE,"QdcXmw05-nOh7-w33V-2QU8-xGgOXz3l01cY"),sQuery(id+"F0.wireOp",EDGE,"wKLpr2SQ-OYyE-akfH-OegQ-YmX1uECdlRNC"),sQuery(id+"F0.wireOp",EDGE,"nIp2yuOM-g37C-dqSd-L2FJ-qzEwNihu1C9F")])]});
            var Q1;
            Q1=makeQuery(id+"F6.boolean.opBoolean","MERGE",EDGE,{"derivedFrom":[makeQuery(id+"F1.opExtrude","SWEPT_EDGE",EDGE,{"disambiguationData":[OSD([sQuery(id+"F0.wireOp",EDGE,"E20.top"),sQuery(id+"F0.wireOp",EDGE,"E20.left")])]}),makeQuery(id+"F6.opExtrude","SWEPT_EDGE",EDGE,{"disambiguationData":[OSD([sQuery(id+"F5.wireOp",EDGE,"E29.top"),sQuery(id+"F5.wireOp",EDGE,"E29.right")])]})]});
            transform(context, id + "F14", {"entities" : qUnion([Q0]), "transformType" : TransformType.ROTATION, "transformAxis" : qUnion([Q1]), "angle" : 90 * degree, "makeCopy" : false});
        }
        {
            var Q0;
            {var subQ0=sQuery(id+"F8EoDyI46MSBQYM_1.wireOp",EDGE,"hDJBzksL-QToe-umQY-51Cy-cnB0OUttW4tD.bottom");var subQ1=sQuery(id+"F8EoDyI46MSBQYM_1.wireOp",EDGE,"pdXBlQge-3E0r-zufv-tM46-rPFQcP1RDKDh.bottom");var subQ2=sQuery(id+"F0.wireOp",EDGE,"nIp2yuOM-g37C-dqSd-L2FJ-qzEwNihu1C9F");var subQ3=sQuery(id+"F0.wireOp",EDGE,"wKLpr2SQ-OYyE-akfH-OegQ-YmX1uECdlRNC");var subQ4=sQuery(id+"F0.wireOp",EDGE,"1ddf9c7e-1f22-45b9-9486-a590a8503efe");var subQ5=sQuery(id+"F0.wireOp",EDGE,"e401b783-9b0b-468a-a8fa-19b962c110bf");var subQ6=sQuery(id+"F0.wireOp",EDGE,"QdcXmw05-nOh7-w33V-2QU8-xGgOXz3l01cY");var subQ7=sQuery(id+"F0.wireOp",EDGE,"vOi8BEkP-FgyD-ud1J-If9y-5dLZR6NiCd4x");var subQ8=sQuery(id+"F0.wireOp",EDGE,"cc97c6fd-5fec-4752-a4a8-6a94110f7a13");var subQ9=sQuery(id+"F0.wireOp",EDGE,"0510f65d-9c0c-41d7-9503-72beef485745");var subQ10=sQuery(id+"F0.wireOp",EDGE,"E28");var subQ11=sQuery(id+"F0.wireOp",EDGE,"E27");var subQ12=sQuery(id+"F0.wireOp",EDGE,"E18");var subQ13=sQuery(id+"F0.wireOp",EDGE,"E13");var subQ14=sQuery(id+"F0.wireOp",EDGE,"E26");var subQ15=sQuery(id+"F0.wireOp",EDGE,"E25");var subQ16=sQuery(id+"F0.wireOp",EDGE,"E19");var subQ17=sQuery(id+"F0.wireOp",EDGE,"E12");var subQ18=sQuery(id+"F0.wireOp",EDGE,"dBvgyE4v-Y0vW-xrYq-FLgZ-j6EjYADPISw6");var subQ19=sQuery(id+"F0.wireOp",EDGE,"ugh5pSRK-4Ctj-t1Pz-bgVR-spiEpQOtgNRe");var subQ20=sQuery(id+"F0.wireOp",EDGE,"86ebaf99-70f6-4ba5-b64b-6db6493a615a");var subQ21=sQuery(id+"F0.wireOp",EDGE,"811e4e27-a576-4234-9d9e-99fd6e5ff174");var subQ22=sQuery(id+"F0.wireOp",EDGE,"6a2Y8GzF-T0tt-Anft-jwha-FWHqF83FpDPI");var subQ23=sQuery(id+"F0.wireOp",EDGE,"uGGpDXvE-blJh-SpWV-2VnG-ZkKB8chZi5NL");var subQ24=sQuery(id+"F0.wireOp",EDGE,"a1f57022-cb78-4938-9068-114398bfe586");var subQ25=sQuery(id+"F0.wireOp",EDGE,"14dc6c6a-b0b1-46ac-8881-e0cf73ac1d2b");var subQ26=sQuery(id+"F0.wireOp",EDGE,"E22");var subQ27=sQuery(id+"F0.wireOp",EDGE,"E21");var subQ28=sQuery(id+"F0.wireOp",EDGE,"E8");var subQ29=sQuery(id+"F0.wireOp",EDGE,"E3");var subQ30=sQuery(id+"F0.wireOp",EDGE,"E24");var subQ31=sQuery(id+"F0.wireOp",EDGE,"E23");var subQ32=sQuery(id+"F0.wireOp",EDGE,"E9");var subQ33=sQuery(id+"F0.wireOp",EDGE,"E2");Q0=makeQuery(id+"FhEWOf1GAh2BQzi_1.boolean.opBoolean","MERGE",FACE,{"derivedFrom":[makeQuery(id+"FwzRGj0mSM9Jiqs_1.boolean.opBoolean","MERGE",FACE,{"derivedFrom":[makeQuery(id+"F3.boolean.opBoolean","MERGE",FACE,{"derivedFrom":[makeQuery(id+"F1.opExtrude","CAP_FACE",FACE,{"disambiguationData":[OSD([sQuery(id+"F0.wireOp",EDGE,"E0"),sQuery(id+"F0.wireOp",EDGE,"E1"),subQ33,subQ29,subQ28,subQ32,sQuery(id+"F0.wireOp",EDGE,"48f8643b-9231-434c-8d4f-c31493e6ee47"),sQuery(id+"F0.wireOp",EDGE,"f29082a4-7322-47cb-b465-19e4ea49e02b"),subQ25,subQ21,subQ20,subQ24,sQuery(id+"F0.wireOp",EDGE,"E10"),sQuery(id+"F0.wireOp",EDGE,"E11"),subQ17,subQ13,subQ12,subQ16,sQuery(id+"F0.wireOp",EDGE,"E20.bottom"),sQuery(id+"F0.wireOp",EDGE,"E20.top"),sQuery(id+"F0.wireOp",EDGE,"E20.left"),sQuery(id+"F0.wireOp",EDGE,"E20.right"),sQuery(id+"F0.wireOp",EDGE,"37bfe060-5fdc-4ec3-b687-e42349816e1c"),sQuery(id+"F0.wireOp",EDGE,"dc5348c1-fa33-4584-8c39-a4fec2a28e45"),subQ9,subQ5,subQ4,subQ8,subQ27,subQ26,subQ31,subQ30,subQ15,subQ14,subQ11,subQ10,subQ19,subQ18,subQ23,subQ22,subQ7,subQ6,subQ3,subQ2])],"isStart":true}),makeQuery(id+"F3.opExtrude","CAP_FACE",FACE,{"disambiguationData":[OSD([subQ33,subQ32,subQ31,subQ30])],"isStart":true}),makeQuery(id+"F3.opExtrude","CAP_FACE",FACE,{"disambiguationData":[OSD([subQ29,subQ28,subQ27,subQ26])],"isStart":true}),makeQuery(id+"F3.opExtrude","CAP_FACE",FACE,{"disambiguationData":[OSD([subQ25,subQ24,subQ23,subQ22])],"isStart":true}),makeQuery(id+"F3.opExtrude","CAP_FACE",FACE,{"disambiguationData":[OSD([subQ21,subQ20,subQ19,subQ18])],"isStart":true}),makeQuery(id+"F3.opExtrude","CAP_FACE",FACE,{"disambiguationData":[OSD([subQ17,subQ16,subQ15,subQ14])],"isStart":true}),makeQuery(id+"F3.opExtrude","CAP_FACE",FACE,{"disambiguationData":[OSD([subQ13,subQ12,subQ11,subQ10])],"isStart":true}),makeQuery(id+"F3.opExtrude","CAP_FACE",FACE,{"disambiguationData":[OSD([subQ9,subQ8,subQ7,subQ6])],"isStart":true}),makeQuery(id+"F3.opExtrude","CAP_FACE",FACE,{"disambiguationData":[OSD([subQ5,subQ4,subQ3,subQ2])],"isStart":true})]}),makeQuery(id+"FwzRGj0mSM9Jiqs_1.opExtrude","SWEPT_FACE",FACE,{"disambiguationData":[OSD([subQ1])]}),makeQuery(id+"FwzRGj0mSM9Jiqs_1.opExtrude","SWEPT_FACE",FACE,{"disambiguationData":[OSD([subQ0])]})]}),makeQuery(id+"FhEWOf1GAh2BQzi_1.opExtrude","SWEPT_FACE",FACE,{"disambiguationData":[OSD([subQ1])]}),makeQuery(id+"FhEWOf1GAh2BQzi_1.opExtrude","SWEPT_FACE",FACE,{"disambiguationData":[OSD([subQ0])]})]});}
            var sketch = newSketch(context, id + "F15", { "sketchPlane" : qUnion([Q0])});
            skLineSegment(sketch, "E36.bottom", {"start": v(65.06, -29.16) * mm, "end": v(30.41, -29.16) * mm});
            skLineSegment(sketch, "E36.top", {"start": v(65.06, -10.16) * mm, "end": v(30.41, -10.16) * mm});
            skLineSegment(sketch, "E36.left", {"start": v(65.06, -29.16) * mm, "end": v(65.06, -10.16) * mm});
            skLineSegment(sketch, "E36.right", {"start": v(30.41, -29.16) * mm, "end": v(30.41, -10.16) * mm});
            skSolve(sketch);
        }
        {
            var Q0;
            {var subQ8=sQuery(id+"F0.wireOp",EDGE,"E0");var subQ26=makeQuery(id+"F1.opExtrude","CAP_EDGE",EDGE,{"disambiguationData":[OSD([subQ8])],"isStart":true});Q0=makeQuery(id+"F15.imprint","IMPRINT",FACE,{"disambiguationData":[TD([[makeQuery(id+"F15.imprint","IMPRINT",EDGE,{"derivedFrom":subQ26}),-1.0]])]});}
            var Q1;
            {var subQ0=sQuery(id+"F15.wireOp",EDGE,"E36.right");var subQ1=sQuery(id+"F15.wireOp",EDGE,"E36.bottom");var subQ2=makeQuery(id+"F15.imprint","INTERSECT",VERTEX,{"derivedFrom":[subQ1,subQ0]});Q1=makeQuery(id+"F15.imprint","IMPRINT",FACE,{"disambiguationData":[TD([[makeQuery(id+"F15.imprint","IMPRINT",EDGE,{"disambiguationData":[TD([[subQ2,1.0]])],"derivedFrom":subQ1}),-1.0]])]});}
            var Q2;
            {var subQ2=sQuery(id+"F15.wireOp",EDGE,"E36.left");Q2=makeQuery(id+"F15.imprint","IMPRINT",FACE,{"disambiguationData":[TD([[makeQuery(id+"F15.imprint","IMPRINT",EDGE,{"derivedFrom":subQ2}),1.0]])]});}
            var Q3;
            {var subQ0=sQuery(id+"F15.wireOp",EDGE,"E36.right");var subQ1=sQuery(id+"F15.wireOp",EDGE,"E36.top");var subQ2=makeQuery(id+"F15.imprint","INTERSECT",VERTEX,{"derivedFrom":[subQ1,subQ0]});Q3=makeQuery(id+"F15.imprint","IMPRINT",FACE,{"disambiguationData":[TD([[makeQuery(id+"F15.imprint","IMPRINT",EDGE,{"disambiguationData":[TD([[subQ2,1.0]])],"derivedFrom":subQ1}),1.0]])]});}
            extrude(context, id + "F16", {"entities" : qUnion([Q0, Q1, Q2, Q3]), "operationType" : NewBodyOperationType.REMOVE, "oppositeDirection" : true, "depth" : 1.5 * mm});
        }
        {
            var Q0;
            Q0=makeQuery(id+"FkJBwdK3IPgQy6d_1.boolean.opBoolean","MERGE",FACE,{"derivedFrom":[makeQuery(id+"F6.opExtrude","SWEPT_FACE",FACE,{"disambiguationData":[OSD([sQuery(id+"F5.wireOp",EDGE,"E29.left")])]}),makeQuery(id+"FkJBwdK3IPgQy6d_1.opExtrude","SWEPT_FACE",FACE,{"disambiguationData":[OSD([sQuery(id+"Fed19Bn8bnM64ZW_1.wireOp",EDGE,"40smzCFM-86pt-zg09-fe2C-5b1X5fqzm7Ba.top")])]})]});
            var sketch = newSketch(context, id + "F17", { "sketchPlane" : qUnion([Q0])});
            skPoint(sketch, "E37", {"position": v(-33.74, -35) * mm});
            skPoint(sketch, "E38", {"position": v(-61.74, -35) * mm});
            skSolve(sketch);
        }
        {
            var Q0;
            Q0=sQuery(id+"F17.wireOp",VERTEX,"E37");
            var Q1;
            Q1=sQuery(id+"F17.wireOp",VERTEX,"E38");
            var Q2;
            Q2=makeQuery(id+"F1.opExtrude","SWEPT_BODY",BODY,{"disambiguationData":[OSD([sQuery(id+"F0.wireOp",EDGE,"E0"),sQuery(id+"F0.wireOp",EDGE,"E1"),sQuery(id+"F0.wireOp",EDGE,"E2"),sQuery(id+"F0.wireOp",EDGE,"E3"),sQuery(id+"F0.wireOp",EDGE,"E8"),sQuery(id+"F0.wireOp",EDGE,"E9"),sQuery(id+"F0.wireOp",EDGE,"48f8643b-9231-434c-8d4f-c31493e6ee47"),sQuery(id+"F0.wireOp",EDGE,"f29082a4-7322-47cb-b465-19e4ea49e02b"),sQuery(id+"F0.wireOp",EDGE,"14dc6c6a-b0b1-46ac-8881-e0cf73ac1d2b"),sQuery(id+"F0.wireOp",EDGE,"811e4e27-a576-4234-9d9e-99fd6e5ff174"),sQuery(id+"F0.wireOp",EDGE,"86ebaf99-70f6-4ba5-b64b-6db6493a615a"),sQuery(id+"F0.wireOp",EDGE,"a1f57022-cb78-4938-9068-114398bfe586"),sQuery(id+"F0.wireOp",EDGE,"E10"),sQuery(id+"F0.wireOp",EDGE,"E11"),sQuery(id+"F0.wireOp",EDGE,"E12"),sQuery(id+"F0.wireOp",EDGE,"E13"),sQuery(id+"F0.wireOp",EDGE,"E18"),sQuery(id+"F0.wireOp",EDGE,"E19"),sQuery(id+"F0.wireOp",EDGE,"E20.bottom"),sQuery(id+"F0.wireOp",EDGE,"E20.top"),sQuery(id+"F0.wireOp",EDGE,"E20.left"),sQuery(id+"F0.wireOp",EDGE,"E20.right"),sQuery(id+"F0.wireOp",EDGE,"37bfe060-5fdc-4ec3-b687-e42349816e1c"),sQuery(id+"F0.wireOp",EDGE,"dc5348c1-fa33-4584-8c39-a4fec2a28e45"),sQuery(id+"F0.wireOp",EDGE,"0510f65d-9c0c-41d7-9503-72beef485745"),sQuery(id+"F0.wireOp",EDGE,"e401b783-9b0b-468a-a8fa-19b962c110bf"),sQuery(id+"F0.wireOp",EDGE,"1ddf9c7e-1f22-45b9-9486-a590a8503efe"),sQuery(id+"F0.wireOp",EDGE,"cc97c6fd-5fec-4752-a4a8-6a94110f7a13"),sQuery(id+"F0.wireOp",EDGE,"E21"),sQuery(id+"F0.wireOp",EDGE,"E22"),sQuery(id+"F0.wireOp",EDGE,"E23"),sQuery(id+"F0.wireOp",EDGE,"E24"),sQuery(id+"F0.wireOp",EDGE,"E25"),sQuery(id+"F0.wireOp",EDGE,"E26"),sQuery(id+"F0.wireOp",EDGE,"E27"),sQuery(id+"F0.wireOp",EDGE,"E28"),sQuery(id+"F0.wireOp",EDGE,"ugh5pSRK-4Ctj-t1Pz-bgVR-spiEpQOtgNRe"),sQuery(id+"F0.wireOp",EDGE,"dBvgyE4v-Y0vW-xrYq-FLgZ-j6EjYADPISw6"),sQuery(id+"F0.wireOp",EDGE,"uGGpDXvE-blJh-SpWV-2VnG-ZkKB8chZi5NL"),sQuery(id+"F0.wireOp",EDGE,"6a2Y8GzF-T0tt-Anft-jwha-FWHqF83FpDPI"),sQuery(id+"F0.wireOp",EDGE,"vOi8BEkP-FgyD-ud1J-If9y-5dLZR6NiCd4x"),sQuery(id+"F0.wireOp",EDGE,"QdcXmw05-nOh7-w33V-2QU8-xGgOXz3l01cY"),sQuery(id+"F0.wireOp",EDGE,"wKLpr2SQ-OYyE-akfH-OegQ-YmX1uECdlRNC"),sQuery(id+"F0.wireOp",EDGE,"nIp2yuOM-g37C-dqSd-L2FJ-qzEwNihu1C9F")])]});
            hole(context, id + "F18", {"style" : HoleStyle.SIMPLE, "endStyle" : HoleEndStyle.THROUGH, "holeDiameter" : 5 * mm, "locations" : qUnion([Q0, Q1]), "scope" : qUnion([Q2]), "isTappedThrough" : true});
        }
        {
            var Q0;
            Q0=makeQuery(id+"FkJBwdK3IPgQy6d_1.boolean.opBoolean","MERGE",FACE,{"derivedFrom":[makeQuery(id+"F6.opExtrude","SWEPT_FACE",FACE,{"disambiguationData":[OSD([sQuery(id+"F5.wireOp",EDGE,"E29.left")])]}),makeQuery(id+"FkJBwdK3IPgQy6d_1.opExtrude","SWEPT_FACE",FACE,{"disambiguationData":[OSD([sQuery(id+"Fed19Bn8bnM64ZW_1.wireOp",EDGE,"40smzCFM-86pt-zg09-fe2C-5b1X5fqzm7Ba.top")])]})]});
            var sketch = newSketch(context, id + "F19", { "sketchPlane" : qUnion([Q0])});
            skText(sketch, "E39", { "text": "RiCkY", "fontName": "OpenSans-Bold.ttf"});
            const initialGuessF19  = {"E39": [-0.06574, -0.00885, 1, 0, 0.00885]};
            skSetInitialGuess(sketch, initialGuessF19);
            skSolve(sketch);
        }
        {
            var Q0;
            Q0 = qSketchRegion(id + "F19", true);
            extrude(context, id + "F20", {"entities" : qUnion([Q0]), "operationType" : NewBodyOperationType.ADD, "depth" : 1 * mm});
        }
        {
            var Q0;
            {var subQ1=sQuery(id+"F5.wireOp",EDGE,"E29.left");var subQ11=sQuery(id+"F0.wireOp",EDGE,"E20.bottom");Q0=makeQuery(id+"F20.boolean.opBoolean","SPLIT",FACE,{"disambiguationData":[TD([makeQuery(id+"F1.opExtrude","SWEPT_FACE",FACE,{"disambiguationData":[OSD([subQ11])]})])],"derivedFrom":makeQuery(id+"F6.opExtrude","SWEPT_FACE",FACE,{"disambiguationData":[OSD([subQ1])]})});}
            var sketch = newSketch(context, id + "F21", { "sketchPlane" : qUnion([Q0])});
            skLineSegment(sketch, "E40.bottom", {"start": v(-67.74, -52) * mm, "end": v(-27.74, -52) * mm});
            skLineSegment(sketch, "E40.top", {"start": v(-67.74, -60) * mm, "end": v(-27.74, -60) * mm});
            skLineSegment(sketch, "E40.left", {"start": v(-67.74, -52) * mm, "end": v(-67.74, -60) * mm});
            skLineSegment(sketch, "E40.right", {"start": v(-27.74, -52) * mm, "end": v(-27.74, -60) * mm});
            skSolve(sketch);
        }
        {
            var Q0;
            Q0=makeQuery(id+"F21.imprint","IMPRINT",FACE,{"disambiguationData":[TD([[makeQuery(id+"F21.imprint","IMPRINT",EDGE,{"derivedFrom":sQuery(id+"F21.wireOp",EDGE,"E40.top")}),1.0]])]});
            extrude(context, id + "F22", {"entities" : qUnion([Q0]), "operationType" : NewBodyOperationType.ADD, "depth" : 14 * mm});
        }
        {
            var Q0;
            Q0=makeQuery(id+"F22.opExtrude","CAP_FACE",FACE,{"disambiguationData":[OSD([sQuery(id+"F21.wireOp",EDGE,"E40.bottom"),sQuery(id+"F21.wireOp",EDGE,"E40.top"),sQuery(id+"F21.wireOp",EDGE,"E40.left"),sQuery(id+"F21.wireOp",EDGE,"E40.right")])],"isStart":false});
            var sketch = newSketch(context, id + "F23", { "sketchPlane" : qUnion([Q0])});
            skLineSegment(sketch, "E41.bottom", {"start": v(-64.74, -52) * mm, "end": v(-59.74, -52) * mm});
            skLineSegment(sketch, "E41.top", {"start": v(-64.74, -60) * mm, "end": v(-59.74, -60) * mm});
            skLineSegment(sketch, "E41.left", {"start": v(-64.74, -52) * mm, "end": v(-64.74, -60) * mm});
            skLineSegment(sketch, "E41.right", {"start": v(-59.74, -52) * mm, "end": v(-59.74, -60) * mm});
            skLineSegment(sketch, "E42.bottom", {"start": v(-47.74, -52) * mm, "end": v(-42.74, -52) * mm});
            skLineSegment(sketch, "E42.top", {"start": v(-47.74, -60) * mm, "end": v(-42.74, -60) * mm});
            skLineSegment(sketch, "E42.left", {"start": v(-47.74, -52) * mm, "end": v(-47.74, -60) * mm});
            skLineSegment(sketch, "E42.right", {"start": v(-42.74, -52) * mm, "end": v(-42.74, -60) * mm});
            skSolve(sketch);
        }
        {
            var Q0;
            Q0=makeQuery(id+"F23.imprint","IMPRINT",FACE,{"disambiguationData":[TD([[makeQuery(id+"F23.imprint","IMPRINT",EDGE,{"derivedFrom":sQuery(id+"F23.wireOp",EDGE,"E41.bottom")}),-1.0]])]});
            var Q1;
            Q1=makeQuery(id+"F23.imprint","IMPRINT",FACE,{"disambiguationData":[TD([[makeQuery(id+"F23.imprint","IMPRINT",EDGE,{"derivedFrom":sQuery(id+"F23.wireOp",EDGE,"E42.bottom")}),-1.0]])]});
            extrude(context, id + "F24", {"entities" : qUnion([Q0, Q1]), "operationType" : NewBodyOperationType.ADD, "depth" : 7 * mm});
        }
        {
            var Q0;
            Q0=makeQuery(id+"F24.boolean.opBoolean","MERGE",FACE,{"derivedFrom":[makeQuery(id+"F22.boolean.opBoolean","MERGE",FACE,{"derivedFrom":[makeQuery(id+"F12.boolean.opBoolean","COPY",FACE,{"derivedFrom":makeQuery(id+"F12.opExtrude","SWEPT_FACE",FACE,{"disambiguationData":[OSD([sQuery(id+"F11.wireOp",EDGE,"E34.top")])]})}),makeQuery(id+"F22.opExtrude","SWEPT_FACE",FACE,{"disambiguationData":[OSD([sQuery(id+"F21.wireOp",EDGE,"E40.bottom")])]})]}),makeQuery(id+"F24.opExtrude","SWEPT_FACE",FACE,{"disambiguationData":[OSD([sQuery(id+"F23.wireOp",EDGE,"E41.bottom")])]}),makeQuery(id+"F24.opExtrude","SWEPT_FACE",FACE,{"disambiguationData":[OSD([sQuery(id+"F23.wireOp",EDGE,"E42.bottom")])]})]});
            extrude(context, id + "F25", {"entities" : qUnion([Q0]), "operationType" : NewBodyOperationType.ADD, "depth" : 2 * mm});
        }
        {
            var Q0;
            Q0=makeQuery(id+"F24.boolean.opBoolean","MERGE",FACE,{"derivedFrom":[makeQuery(id+"F22.boolean.opBoolean","MERGE",FACE,{"derivedFrom":[makeQuery(id+"F6.opExtrude","CAP_FACE",FACE,{"disambiguationData":[OSD([sQuery(id+"F5.wireOp",EDGE,"E29.bottom"),sQuery(id+"F5.wireOp",EDGE,"E29.top"),sQuery(id+"F5.wireOp",EDGE,"E29.left"),sQuery(id+"F5.wireOp",EDGE,"E29.right")])],"isStart":false}),makeQuery(id+"F22.opExtrude","SWEPT_FACE",FACE,{"disambiguationData":[OSD([sQuery(id+"F21.wireOp",EDGE,"E40.top")])]})]}),makeQuery(id+"F24.opExtrude","SWEPT_FACE",FACE,{"disambiguationData":[OSD([sQuery(id+"F23.wireOp",EDGE,"E41.top")])]}),makeQuery(id+"F24.opExtrude","SWEPT_FACE",FACE,{"disambiguationData":[OSD([sQuery(id+"F23.wireOp",EDGE,"E42.top")])]})]});
            var sketch = newSketch(context, id + "F26", { "sketchPlane" : qUnion([Q0])});
            skLineSegment(sketch, "E43.bottom", {"start": v(35.74, -1.16) * mm, "end": v(59.74, -1.16) * mm});
            skLineSegment(sketch, "E43.top", {"start": v(35.74, -8.16) * mm, "end": v(59.74, -8.16) * mm});
            skLineSegment(sketch, "E43.left", {"start": v(35.74, 1.84) * mm, "end": v(35.74, -8.16) * mm});
            skLineSegment(sketch, "E43.right", {"start": v(59.74, 1.84) * mm, "end": v(59.74, -8.16) * mm});
            skSolve(sketch);
        }
        {
            var Q0;
            Q0 = qSketchRegion(id + "F26", true);
            extrude(context, id + "F27", {"entities" : qUnion([Q0]), "operationType" : NewBodyOperationType.REMOVE, "oppositeDirection" : true, "depth" : 11 * mm});
        }
        {
            var Q0;
            {var subQ0=sQuery(id+"F23.wireOp",EDGE,"E41.left");Q0=makeQuery(id+"F25.boolean.opBoolean","MERGE",FACE,{"derivedFrom":[makeQuery(id+"F24.opExtrude","SWEPT_FACE",FACE,{"disambiguationData":[OSD([subQ0])]}),makeQuery(id+"F25.opExtrude","SWEPT_FACE",FACE,{"disambiguationData":[OSD([sQuery(id+"F21.wireOp",EDGE,"E40.bottom"),sQuery(id+"F23.wireOp",EDGE,"E41.bottom"),subQ0])]})]});}
            var sketch = newSketch(context, id + "F28", { "sketchPlane" : qUnion([Q0])});
            skLineSegment(sketch, "E44.bottom", {"start": v(19.16, -53) * mm, "end": v(15.16, -53) * mm});
            skLineSegment(sketch, "E44.top", {"start": v(19.16, -57) * mm, "end": v(15.16, -57) * mm});
            skLineSegment(sketch, "E44.left", {"start": v(19.16, -53) * mm, "end": v(19.16, -57) * mm});
            skLineSegment(sketch, "E44.right", {"start": v(15.16, -53) * mm, "end": v(15.16, -57) * mm});
            skSolve(sketch);
        }
        {
            var Q0;
            Q0 = qSketchRegion(id + "F28", true);
            var Q1;
            Q1=makeQuery(id+"F28.imprint","IMPRINT",FACE,{"disambiguationData":[TD([[makeQuery(id+"F28.imprint","IMPRINT",EDGE,{"derivedFrom":sQuery(id+"F28.wireOp",EDGE,"E44.bottom")}),1.0]])]});
            extrude(context, id + "F29", {"entities" : qUnion([Q0, Q1]), "operationType" : NewBodyOperationType.REMOVE, "oppositeDirection" : true, "depth" : 25 * mm});
        }
        {
            var Q0;
            Q0=makeQuery(id+"F9.opExtrude","CAP_FACE",FACE,{"disambiguationData":[OSD([sQuery(id+"F7.wireOp",EDGE,"E30"),sQuery(id+"F7.wireOp",EDGE,"E31"),sQuery(id+"F7.wireOp",EDGE,"E32")])],"isStart":false});
            extrude(context, id + "F30", {"entities" : qUnion([Q0]), "operationType" : NewBodyOperationType.ADD, "depth" : .5 * mm});
        }
        {
            var Q0;
            Q0=makeQuery(id+"F10.opExtrude","CAP_FACE",FACE,{"disambiguationData":[OSD([sQuery(id+"F0.wireOp",EDGE,"E20.top"),sQuery(id+"F5.wireOp",EDGE,"E29.top"),sQuery(id+"F5.wireOp",EDGE,"E29.left"),sQuery(id+"F8.wireOp",EDGE,"E33")])],"isStart":false});
            extrude(context, id + "F31", {"entities" : qUnion([Q0]), "operationType" : NewBodyOperationType.ADD, "depth" : .5 * mm});
        }
        {
            var Q0;
            {var subQ0=sQuery(id+"F21.wireOp",EDGE,"E40.right");var subQ1=sQuery(id+"F21.wireOp",EDGE,"E40.bottom");var subQ2=sQuery(id+"F5.wireOp",EDGE,"E29.left");var subQ3=sQuery(id+"F5.wireOp",EDGE,"E29.top");var subQ4=sQuery(id+"F0.wireOp",EDGE,"E20.top");Q0=makeQuery(id+"F25.boolean.opBoolean","MERGE",EDGE,{"derivedFrom":[makeQuery(id+"F22.opExtrude","CAP_EDGE",EDGE,{"disambiguationData":[OSD([subQ0])],"isStart":false}),makeQuery(id+"F25.opExtrude","SWEPT_EDGE",EDGE,{"disambiguationData":[OSD([subQ4,subQ3,subQ2,subQ1,subQ0]),TDD([makeQuery(id+"F22.opExtrude","CAP_VERTEX",VERTEX,{"disambiguationData":[OSD([subQ4,subQ3,subQ2,subQ1,subQ0])],"isStart":false})])]})]});}
            var Q1;
            {var subQ0=sQuery(id+"F21.wireOp",EDGE,"E40.left");var subQ1=sQuery(id+"F21.wireOp",EDGE,"E40.bottom");var subQ2=sQuery(id+"F5.wireOp",EDGE,"E29.left");var subQ3=sQuery(id+"F5.wireOp",EDGE,"E29.bottom");var subQ4=sQuery(id+"F0.wireOp",EDGE,"E20.bottom");Q1=makeQuery(id+"F25.boolean.opBoolean","MERGE",EDGE,{"derivedFrom":[makeQuery(id+"F22.opExtrude","CAP_EDGE",EDGE,{"disambiguationData":[OSD([subQ0])],"isStart":false}),makeQuery(id+"F25.opExtrude","SWEPT_EDGE",EDGE,{"disambiguationData":[OSD([subQ4,subQ3,subQ2,subQ1,subQ0]),TDD([makeQuery(id+"F22.opExtrude","CAP_VERTEX",VERTEX,{"disambiguationData":[OSD([subQ4,subQ3,subQ2,subQ1,subQ0])],"isStart":false})])]})]});}
            fillet(context, id + "F32", {"entities" : qUnion([Q0, Q1]), "radius" : 3 * mm, "tangentPropagation" : true, "allowEdgeOverflow" : false});
        }
        {
            var Q0;
            Q0=makeQuery(id+"F24.opExtrude","CAP_EDGE",EDGE,{"disambiguationData":[OSD([sQuery(id+"F23.wireOp",EDGE,"E41.top")])],"isStart":false});
            var Q1;
            Q1=makeQuery(id+"F25.opExtrude","CAP_EDGE",EDGE,{"disambiguationData":[OSD([sQuery(id+"F23.wireOp",EDGE,"E41.bottom")])],"isStart":false});
            var Q2;
            Q2=makeQuery(id+"F24.opExtrude","CAP_EDGE",EDGE,{"disambiguationData":[OSD([sQuery(id+"F23.wireOp",EDGE,"E42.top")])],"isStart":false});
            var Q3;
            Q3=makeQuery(id+"F25.opExtrude","CAP_EDGE",EDGE,{"disambiguationData":[OSD([sQuery(id+"F23.wireOp",EDGE,"E42.bottom")])],"isStart":false});
            var Q4;
            {var subQ0=sQuery(id+"F23.wireOp",EDGE,"E41.left");var subQ1=sQuery(id+"F21.wireOp",EDGE,"E40.bottom");var subQ2=sQuery(id+"F21.wireOp",EDGE,"E40.left");var subQ3=sQuery(id+"F5.wireOp",EDGE,"E29.left");var subQ4=sQuery(id+"F5.wireOp",EDGE,"E29.bottom");var subQ5=sQuery(id+"F0.wireOp",EDGE,"E20.bottom");Q4=makeQuery(id+"F32.opFillet","BLEND_EDGE",EDGE,{"disambiguationData":[OD(0.0)],"blendedFrom":[makeQuery(id+"F25.boolean.opBoolean","MERGE",EDGE,{"derivedFrom":[makeQuery(id+"F22.opExtrude","CAP_EDGE",EDGE,{"disambiguationData":[OSD([subQ2])],"isStart":false}),makeQuery(id+"F25.opExtrude","SWEPT_EDGE",EDGE,{"disambiguationData":[OSD([subQ5,subQ4,subQ3,subQ1,subQ2]),TDD([makeQuery(id+"F22.opExtrude","CAP_VERTEX",VERTEX,{"disambiguationData":[OSD([subQ5,subQ4,subQ3,subQ1,subQ2])],"isStart":false})])]})]}),makeQuery(id+"F25.boolean.opBoolean","MERGE",FACE,{"derivedFrom":[makeQuery(id+"F24.opExtrude","SWEPT_FACE",FACE,{"disambiguationData":[OSD([subQ0])]}),makeQuery(id+"F25.opExtrude","SWEPT_FACE",FACE,{"disambiguationData":[OSD([subQ1,sQuery(id+"F23.wireOp",EDGE,"E41.bottom"),subQ0])]})]})],"blendedInto":[makeQuery(id+"F25.boolean.opBoolean","MERGE",FACE,{"derivedFrom":[makeQuery(id+"F24.opExtrude","SWEPT_FACE",FACE,{"disambiguationData":[OSD([subQ0])]}),makeQuery(id+"F25.opExtrude","SWEPT_FACE",FACE,{"disambiguationData":[OSD([subQ1,sQuery(id+"F23.wireOp",EDGE,"E41.bottom"),subQ0])]})]})]});}
            var Q5;
            {var subQ0=sQuery(id+"F23.wireOp",EDGE,"E41.left");var subQ1=sQuery(id+"F21.wireOp",EDGE,"E40.bottom");var subQ2=sQuery(id+"F21.wireOp",EDGE,"E40.left");var subQ3=sQuery(id+"F5.wireOp",EDGE,"E29.left");var subQ4=sQuery(id+"F5.wireOp",EDGE,"E29.bottom");var subQ5=sQuery(id+"F0.wireOp",EDGE,"E20.bottom");Q5=makeQuery(id+"F32.opFillet","BLEND_EDGE",EDGE,{"disambiguationData":[OD(1.0)],"blendedFrom":[makeQuery(id+"F25.boolean.opBoolean","MERGE",EDGE,{"derivedFrom":[makeQuery(id+"F22.opExtrude","CAP_EDGE",EDGE,{"disambiguationData":[OSD([subQ2])],"isStart":false}),makeQuery(id+"F25.opExtrude","SWEPT_EDGE",EDGE,{"disambiguationData":[OSD([subQ5,subQ4,subQ3,subQ1,subQ2]),TDD([makeQuery(id+"F22.opExtrude","CAP_VERTEX",VERTEX,{"disambiguationData":[OSD([subQ5,subQ4,subQ3,subQ1,subQ2])],"isStart":false})])]})]}),makeQuery(id+"F25.boolean.opBoolean","MERGE",FACE,{"derivedFrom":[makeQuery(id+"F24.opExtrude","SWEPT_FACE",FACE,{"disambiguationData":[OSD([subQ0])]}),makeQuery(id+"F25.opExtrude","SWEPT_FACE",FACE,{"disambiguationData":[OSD([subQ1,sQuery(id+"F23.wireOp",EDGE,"E41.bottom"),subQ0])]})]})],"blendedInto":[makeQuery(id+"F25.boolean.opBoolean","MERGE",FACE,{"derivedFrom":[makeQuery(id+"F24.opExtrude","SWEPT_FACE",FACE,{"disambiguationData":[OSD([subQ0])]}),makeQuery(id+"F25.opExtrude","SWEPT_FACE",FACE,{"disambiguationData":[OSD([subQ1,sQuery(id+"F23.wireOp",EDGE,"E41.bottom"),subQ0])]})]})]});}
            var Q6;
            {var subQ0=sQuery(id+"F23.wireOp",EDGE,"E41.bottom");var subQ2=sQuery(id+"F21.wireOp",EDGE,"E40.bottom");var subQ6=sQuery(id+"F21.wireOp",EDGE,"E40.top");var subQ8=sQuery(id+"F23.wireOp",EDGE,"E41.right");Q6=makeQuery(id+"F29.boolean.opBoolean","SPLIT",EDGE,{"disambiguationData":[TD([makeQuery(id+"F22.opExtrude","SWEPT_FACE",FACE,{"disambiguationData":[OSD([subQ6])]})])],"derivedFrom":makeQuery(id+"F25.boolean.opBoolean","MERGE",EDGE,{"derivedFrom":[makeQuery(id+"F24.opExtrude","CAP_EDGE",EDGE,{"disambiguationData":[OSD([subQ8])],"isStart":true}),makeQuery(id+"F25.opExtrude","SWEPT_EDGE",EDGE,{"disambiguationData":[OSD([subQ2,subQ0,subQ8]),TDD([makeQuery(id+"F24.opExtrude","CAP_VERTEX",VERTEX,{"disambiguationData":[OSD([subQ2,subQ0,subQ8])],"isStart":true})])]})]})});}
            var Q7;
            {var subQ6=sQuery(id+"F21.wireOp",EDGE,"E40.bottom");var subQ9=sQuery(id+"F23.wireOp",EDGE,"E41.bottom");var subQ14=sQuery(id+"F23.wireOp",EDGE,"E41.right");Q7=makeQuery(id+"F29.boolean.opBoolean","SPLIT",EDGE,{"disambiguationData":[TD([makeQuery(id+"F29.opExtrude","SWEPT_FACE",FACE,{"disambiguationData":[OSD([sQuery(id+"F28.wireOp",EDGE,"E44.bottom")])]})])],"derivedFrom":makeQuery(id+"F25.boolean.opBoolean","MERGE",EDGE,{"derivedFrom":[makeQuery(id+"F24.opExtrude","CAP_EDGE",EDGE,{"disambiguationData":[OSD([subQ14])],"isStart":true}),makeQuery(id+"F25.opExtrude","SWEPT_EDGE",EDGE,{"disambiguationData":[OSD([subQ6,subQ9,subQ14]),TDD([makeQuery(id+"F24.opExtrude","CAP_VERTEX",VERTEX,{"disambiguationData":[OSD([subQ6,subQ9,subQ14])],"isStart":true})])]})]})});}
            var Q8;
            {var subQ5=sQuery(id+"F21.wireOp",EDGE,"E40.top");var subQ6=sQuery(id+"F21.wireOp",EDGE,"E40.bottom");var subQ9=sQuery(id+"F23.wireOp",EDGE,"E42.bottom");var subQ15=sQuery(id+"F23.wireOp",EDGE,"E42.right");Q8=makeQuery(id+"F29.boolean.opBoolean","SPLIT",EDGE,{"disambiguationData":[TD([makeQuery(id+"F22.opExtrude","SWEPT_FACE",FACE,{"disambiguationData":[OSD([subQ5])]})])],"derivedFrom":makeQuery(id+"F25.boolean.opBoolean","MERGE",EDGE,{"derivedFrom":[makeQuery(id+"F24.opExtrude","CAP_EDGE",EDGE,{"disambiguationData":[OSD([subQ15])],"isStart":true}),makeQuery(id+"F25.opExtrude","SWEPT_EDGE",EDGE,{"disambiguationData":[OSD([subQ6,subQ9,subQ15]),TDD([makeQuery(id+"F24.opExtrude","CAP_VERTEX",VERTEX,{"disambiguationData":[OSD([subQ6,subQ9,subQ15])],"isStart":true})])]})]})});}
            var Q9;
            {var subQ6=sQuery(id+"F21.wireOp",EDGE,"E40.bottom");var subQ11=sQuery(id+"F23.wireOp",EDGE,"E42.bottom");var subQ13=sQuery(id+"F23.wireOp",EDGE,"E42.right");Q9=makeQuery(id+"F29.boolean.opBoolean","SPLIT",EDGE,{"disambiguationData":[TD([makeQuery(id+"F29.opExtrude","SWEPT_FACE",FACE,{"disambiguationData":[OSD([sQuery(id+"F28.wireOp",EDGE,"E44.bottom")])]})])],"derivedFrom":makeQuery(id+"F25.boolean.opBoolean","MERGE",EDGE,{"derivedFrom":[makeQuery(id+"F24.opExtrude","CAP_EDGE",EDGE,{"disambiguationData":[OSD([subQ13])],"isStart":true}),makeQuery(id+"F25.opExtrude","SWEPT_EDGE",EDGE,{"disambiguationData":[OSD([subQ6,subQ11,subQ13]),TDD([makeQuery(id+"F24.opExtrude","CAP_VERTEX",VERTEX,{"disambiguationData":[OSD([subQ6,subQ11,subQ13])],"isStart":true})])]})]})});}
            var Q10;
            {var subQ1=sQuery(id+"F21.wireOp",EDGE,"E40.bottom");var subQ3=sQuery(id+"F23.wireOp",EDGE,"E42.left");var subQ7=sQuery(id+"F21.wireOp",EDGE,"E40.top");var subQ10=sQuery(id+"F23.wireOp",EDGE,"E42.bottom");Q10=makeQuery(id+"F29.boolean.opBoolean","SPLIT",EDGE,{"disambiguationData":[TD([makeQuery(id+"F22.opExtrude","SWEPT_FACE",FACE,{"disambiguationData":[OSD([subQ7])]})])],"derivedFrom":makeQuery(id+"F25.boolean.opBoolean","MERGE",EDGE,{"derivedFrom":[makeQuery(id+"F24.opExtrude","CAP_EDGE",EDGE,{"disambiguationData":[OSD([subQ3])],"isStart":true}),makeQuery(id+"F25.opExtrude","SWEPT_EDGE",EDGE,{"disambiguationData":[OSD([subQ1,subQ10,subQ3]),TDD([makeQuery(id+"F24.opExtrude","CAP_VERTEX",VERTEX,{"disambiguationData":[OSD([subQ1,subQ10,subQ3])],"isStart":true})])]})]})});}
            var Q11;
            {var subQ6=sQuery(id+"F21.wireOp",EDGE,"E40.bottom");var subQ11=sQuery(id+"F23.wireOp",EDGE,"E42.bottom");var subQ14=sQuery(id+"F23.wireOp",EDGE,"E42.left");Q11=makeQuery(id+"F29.boolean.opBoolean","SPLIT",EDGE,{"disambiguationData":[TD([makeQuery(id+"F29.opExtrude","SWEPT_FACE",FACE,{"disambiguationData":[OSD([sQuery(id+"F28.wireOp",EDGE,"E44.bottom")])]})])],"derivedFrom":makeQuery(id+"F25.boolean.opBoolean","MERGE",EDGE,{"derivedFrom":[makeQuery(id+"F24.opExtrude","CAP_EDGE",EDGE,{"disambiguationData":[OSD([subQ14])],"isStart":true}),makeQuery(id+"F25.opExtrude","SWEPT_EDGE",EDGE,{"disambiguationData":[OSD([subQ6,subQ11,subQ14]),TDD([makeQuery(id+"F24.opExtrude","CAP_VERTEX",VERTEX,{"disambiguationData":[OSD([subQ6,subQ11,subQ14])],"isStart":true})])]})]})});}
            fillet(context, id + "F33", {"entities" : qUnion([Q0, Q1, Q2, Q3, Q4, Q5, Q6, Q7, Q8, Q9, Q10, Q11]), "radius" : 2 * mm, "tangentPropagation" : true, "allowEdgeOverflow" : false});
        }
        {
            var Q0;
            {var subQ1=sQuery(id+"F5.wireOp",EDGE,"E29.left");var subQ11=sQuery(id+"F0.wireOp",EDGE,"E20.bottom");Q0=makeQuery(id+"F27.boolean.opBoolean","MERGE",FACE,{"derivedFrom":[makeQuery(id+"F20.boolean.opBoolean","SPLIT",FACE,{"disambiguationData":[TD([makeQuery(id+"F1.opExtrude","SWEPT_FACE",FACE,{"disambiguationData":[OSD([subQ11])]})])],"derivedFrom":makeQuery(id+"F6.opExtrude","SWEPT_FACE",FACE,{"disambiguationData":[OSD([subQ1])]})}),makeQuery(id+"F27.opExtrude","SWEPT_FACE",FACE,{"disambiguationData":[OSD([sQuery(id+"F26.wireOp",EDGE,"E43.bottom")])]})]});}
            var sketch = newSketch(context, id + "F34", { "sketchPlane" : qUnion([Q0])});
            skText(sketch, "E45", { "text": "V.2", "fontName": "OpenSans-Bold.ttf"});
            const initialGuessF34  = {"E45": [-0.0393, -0.01496, 1, 0, 0.00424]};
            skSetInitialGuess(sketch, initialGuessF34);
            skSolve(sketch);
        }
        {
            var Q0;
            Q0 = qSketchRegion(id + "F34", true);
            extrude(context, id + "F35", {"entities" : qUnion([Q0]), "operationType" : NewBodyOperationType.ADD, "depth" : 1 * mm});
        }
    });
